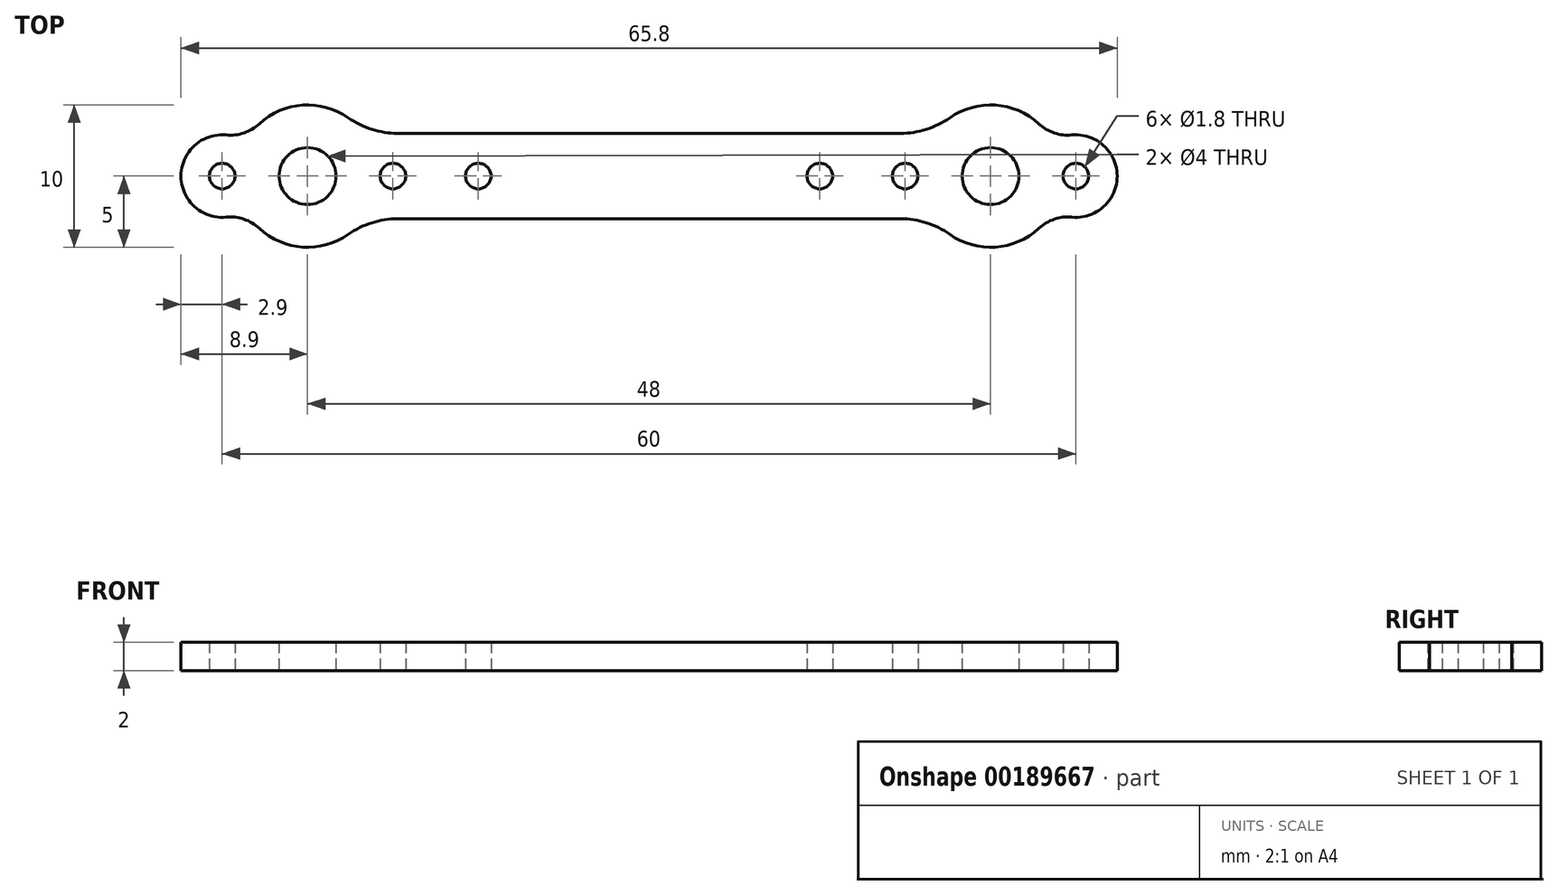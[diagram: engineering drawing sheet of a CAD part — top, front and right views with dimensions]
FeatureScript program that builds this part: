
annotation { "Feature Type Name" : "Feature", "Feature Type Description" : "" }
export const myFeature = defineFeature(function(context is Context, id is Id, definition is map)
    precondition{}
    {
        {
            var Q0;
            Q0=qCreatedBy(makeId("Top.planeOp"),FACE);
            var sketch = newSketch(context, id + "F0", { "sketchPlane" : qUnion([Q0])});
            skLineSegment(sketch, "E0", {"start": v(0, 0) * mm, "end": v(-24, 0) * mm, "construction": true});
            skCircle(sketch, "E1", {"center": v(-24, 0) * mm, "radius": 2 * mm});
            skCircle(sketch, "E2", {"center": v(-18, 0) * mm, "radius": 0.9 * mm});
            skCircle(sketch, "E3", {"center": v(-12, 0) * mm, "radius": 0.9 * mm});
            skCircle(sketch, "E4", {"center": v(-30, 0) * mm, "radius": 0.9 * mm});
            skLineSegment(sketch, "E5", {"start": v(0, 3) * mm, "end": v(-17.68, 3) * mm});
            skLineSegment(sketch, "E6.MirrorCS", {"start": v(0, -3) * mm, "end": v(-17.68, -3) * mm});
            skArc(sketch, "E7.0", {"start": v(-27.4, -3.67) * mm, "mid": v(-24.33, -4.99) * mm, "end": v(-21.13, -4.1) * mm});
            skArc(sketch, "E8.0", {"start": v(-29.72, 2.89) * mm, "mid": v(-32.9, 0) * mm, "end": v(-29.72, -2.89) * mm});
            skArc(sketch, "E9.trimOffspring", {"start": v(-21.13, 4.1) * mm, "mid": v(-24.33, 4.99) * mm, "end": v(-27.4, 3.67) * mm});
            skPoint(sketch, "E10.orphan", {"position": v(-20.58, 3) * mm});
            skPoint(sketch, "E11.orphan", {"position": v(-20.58, -3) * mm});
            skPoint(sketch, "E12.visualSharp", {"position": v(-20, 3) * mm});
            skArc(sketch, "E12.filletArc", {"start": v(-21.13, 4.1) * mm, "mid": v(-19.48, 3.28) * mm, "end": v(-17.68, 3) * mm});
            skPoint(sketch, "E13.visualSharp", {"position": v(-20, -3) * mm});
            skArc(sketch, "E13.filletArc", {"start": v(-17.68, -3) * mm, "mid": v(-19.48, -3.28) * mm, "end": v(-21.13, -4.1) * mm});
            skPoint(sketch, "E14.visualSharp", {"position": v(-28.38, 2.4) * mm});
            skArc(sketch, "E14.filletArc", {"start": v(-29.72, 2.89) * mm, "mid": v(-28.47, 3.03) * mm, "end": v(-27.4, 3.67) * mm});
            skPoint(sketch, "E15.visualSharp", {"position": v(-28.38, -2.4) * mm});
            skArc(sketch, "E15.filletArc", {"start": v(-27.4, -3.67) * mm, "mid": v(-28.47, -3.03) * mm, "end": v(-29.72, -2.89) * mm});
            skLineSegment(sketch, "E16", {"start": v(0, 0) * mm, "end": v(0, 11) * mm, "construction": true});
            skLineSegment(sketch, "E17.MirrorCS", {"start": v(0, 3) * mm, "end": v(17.68, 3) * mm});
            skArc(sketch, "E18.MirrorCS", {"start": v(21.13, 4.1) * mm, "mid": v(19.48, 3.28) * mm, "end": v(17.68, 3) * mm});
            skArc(sketch, "E19.MirrorCS", {"start": v(21.13, 4.1) * mm, "mid": v(24.33, 4.99) * mm, "end": v(27.4, 3.67) * mm});
            skArc(sketch, "E20.MirrorCS", {"start": v(29.72, 2.89) * mm, "mid": v(28.47, 3.03) * mm, "end": v(27.4, 3.67) * mm});
            skArc(sketch, "E21.MirrorCS", {"start": v(29.72, 2.89) * mm, "mid": v(32.9, 0) * mm, "end": v(29.72, -2.89) * mm});
            skArc(sketch, "E22.MirrorCS", {"start": v(27.4, -3.67) * mm, "mid": v(28.47, -3.03) * mm, "end": v(29.72, -2.89) * mm});
            skArc(sketch, "E23.MirrorCS", {"start": v(27.4, -3.67) * mm, "mid": v(24.33, -4.99) * mm, "end": v(21.13, -4.1) * mm});
            skArc(sketch, "E24.MirrorCS", {"start": v(17.68, -3) * mm, "mid": v(19.48, -3.28) * mm, "end": v(21.13, -4.1) * mm});
            skLineSegment(sketch, "E25.MirrorCS", {"start": v(0, -3) * mm, "end": v(17.68, -3) * mm});
            skCircle(sketch, "E26.MirrorC", {"center": v(12, 0) * mm, "radius": 0.9 * mm});
            skCircle(sketch, "E27.MirrorC", {"center": v(18, 0) * mm, "radius": 0.9 * mm});
            skCircle(sketch, "E28.MirrorC", {"center": v(24, 0) * mm, "radius": 2 * mm});
            skCircle(sketch, "E29.MirrorC", {"center": v(30, 0) * mm, "radius": 0.9 * mm});
            skSolve(sketch);
        }
        {
            var Q0;
            Q0=makeQuery(id+"F0.imprint","IMPRINT",FACE,{"disambiguationData":[TD([[makeQuery(id+"F0.imprint","IMPRINT",EDGE,{"derivedFrom":sQuery(id+"F0.wireOp",EDGE,"E1")}),-1.0]])]});
            extrude(context, id + "F1", {"entities" : qUnion([Q0]), "depth" : 2 * mm});
        }
    });
